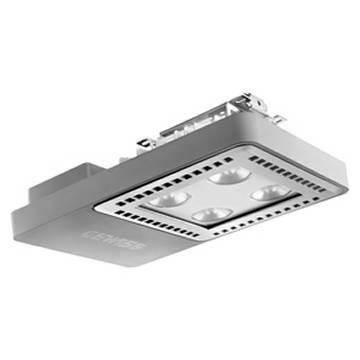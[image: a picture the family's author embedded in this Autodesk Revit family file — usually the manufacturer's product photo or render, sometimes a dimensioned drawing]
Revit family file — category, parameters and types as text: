
# Revit family: Lighting-Industriale-GEWISS-SMART[4]HE_APPARECCHI-LED_1M
name_source: partatom
category: Apparecchi per illuminazione
units: mm (PartAtom-declared; Revit-internal decimal feet)

## family parameters
Basato su piano di lavoro = Sì
Condiviso = No
Numero OmniClass = 23.80.00.00
Punto di calcolo locali = Sì
Quota connettore circolare = Usa diametro
Sempre verticale = No
Sorgente d'illuminazione = No
Taglio con vuoti quando caricato = No
Tipo di parte = Normale
Titolo OmniClass = Electric Power and Lighting

## types (1)
- Lighting-Industriale-GEWISS-SMART[4]HE_APPARECCHI-LED_1M
    Alimentatore = Incluso
    Apparecchio a ridotta temperatura superficiale = Si
    Applicazione = Interno
    Cablaggio = Con connettore stagno Gw connect
    Caratteristiche elettriche e gestione della luce = -
    Caratteristiche ottiche e illuminotecniche = -
    Carico apparente = 50 VA
    Catalogo = LIGHTING
    Certificazione DIN 18032-3 = Con Staffa - Kit Funi + morsetto (in approvazione)
    Certificazioni e classificazioni = -
    Classe fotobiologica = RG0
    Classe isolamento = I
    Classificazione = Lighting
    Classificazione: = -
    Codice Electrocod = 2444
    Codice digitale univoco (Datamatrix) = Datamatrix
    Colore = Grigio RAL 7035
    Commenti sul wattaggio = 50W
    Contesto = Illuminazione di logistiche e locali produttivi industriali
    Controllo abbagliamento e luminanza = -
    Corpo = PA6 “Halogen Free” caricato fibra vetro
    Descrizione = SMART[4]LB 1M C.PAS.ON/OFF ELL.57K
    Dispositivo di protezione = DM 6kV / CM 6kV
    Distanza tot_plafoniera = 74 mm  [stored 0.242782 ft]
    Durata di vita = L90B10 (Tq+25°C) = 70.000 h - L90B10 (Tq+50°C) = 35.000 h
    Efficienza luminosa (lm/W) = 131
    Finitura colore = Grigio RAL 7035
    Fissaggio = -
    Frequenza nominale (Hz) = 50/60 Hz
    Gancio di chiusura = -
    Garanzia = 5 anni
    Grado di protezione = IP66
    Gruppo ottico = Riflettore in PC metallizzato e lenti in PMMA
    Guarnizioni = tipo siliconico antinvecchiamento
    IDF = 1c7b1567-d3fc-4f8d-b279-2371ae55e86b
    IDT = 33be10311be341e0b261e3e80f29047b
    IPEA = -
    Immagine tipo = GWL1071.jpg
    Inclinazione = Con accessorio staffa
    Indice di resa cromatica = CRI-80
    Informazioni generali = -
    Installazione e manutenzione = -
    Lampada = LED
    Larghezza = 253 mm  [stored 0.830052 ft]
    Lumen output (lm) = 6300
    Lunghezza = 383 mm  [stored 1.25656 ft]
    Materiali = -
    Modello = GWS4122AQ857
    Motore = <Per categoria>
    Norma di riferimento = EN 60598-1 ; EN 60598-2-1 ; EN 60598-2-24
    Ottica = Ellittica
    Peso (kg): = 3,5
    Plafoniera = <Per categoria>
    Potenza di sistema = 48W
    Produttore = GEWISS S.p.A.
    Prospetto di default = 1219 mm
    Raggio led = 30 mm  [stored 0.0984252 ft]
    Resistenza agli urti = IK08
    Resistenza al filo incandescente = 850 °C
    SEO = Low Bay
    Scheda Tecnica = https://www.gewiss.com
    Schermo = Vetro Temprato Spessore 4mm
    Sistema di controllo = ON / OFF
    Sistema di controllo : = ON / OFF
    Sostituibilità gruppo ottico = Non sostituibile
    Sostituibilità piastra di cablaggio = Non sostituibile
    Spessore plafoniera = 40 mm  [stored 0.131234 ft]
    Superficie massima esposta al vento : = 0,097 m²
    Temperatura di colore = 5700K
    Temperatura di esercizio = -30°C ÷ +50 °C
    Temperatura di stoccaggio = -40 +70 °C
    Tensione di alimentazione = 220 - 240 V
    Tipo di apparecchio = Riflettore industriale a LED&nbsp;
    Tipo di installazione e montaggio = Plafone - Parete - Sospensione
    Tipologia sorgente luminosa = LED - Non sostituibile
    Tolleranza cromatica = SDCM = 3
    Trasformatore = <Per categoria>
    URL = https://www.gewiss.com
    Vano di alimentazione = Integrato
    Versione file RFA = 20.11
    Vetro acceso = Lampada accesa
    Viti esterne = Acciaio inox
    Voltaggio = 230 V

note: [stored X ft] marks values corroborated as IEEE doubles in the binary element streams (Revit-internal decimal feet)

## geometry (parser evidence)
native form markers: Blend x4
no freeform markers — native parametric forms only
